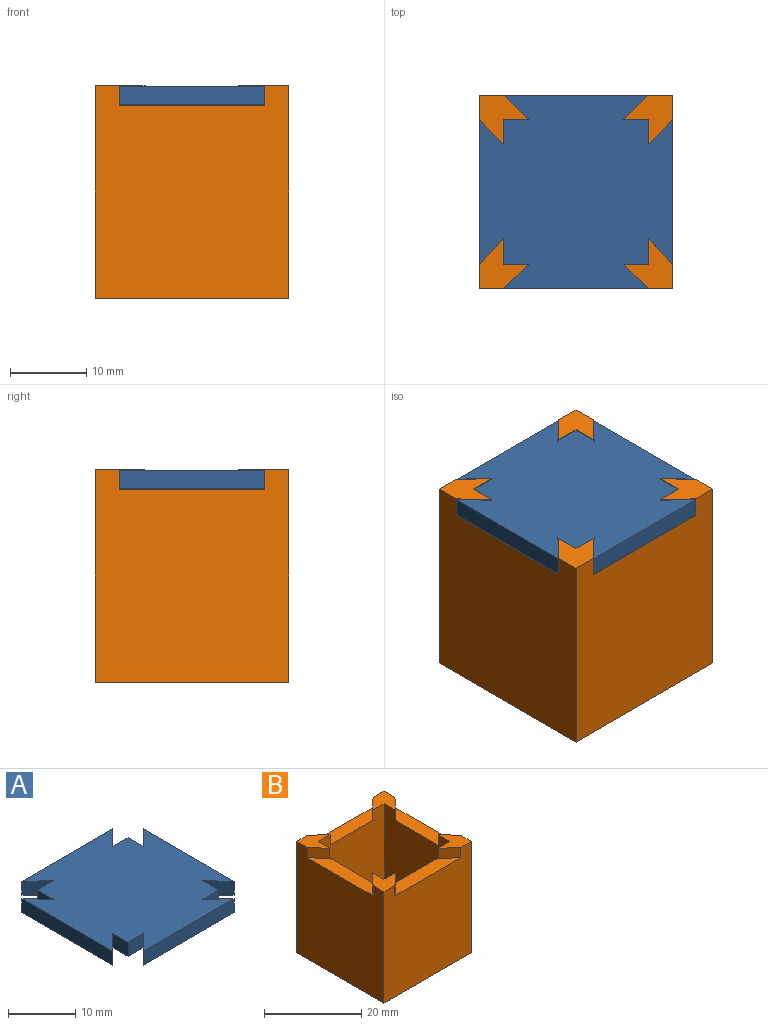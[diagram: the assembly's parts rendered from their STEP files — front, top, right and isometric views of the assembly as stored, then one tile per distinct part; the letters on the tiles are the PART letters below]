
ASSEMBLY  parts=2 mates=1
PART A: 22 faces, bbox 25.4x25.4x2.5 mm
  f0: plane 3.35x3.18mm, normal (-0.69,-0.73,0), area 11.7mm2, adj f1,f19,f20,f21
  f1: plane 3.35x2.54mm, normal (0,1,0), area 8.5mm2, adj f0,f2,f20,f21
  f2: plane 3.35x2.54mm, normal (-1,0,0), area 8.5mm2, adj f1,f3,f20,f21
  f3: plane 3.35x3.18mm, normal (0.73,0.69,0), area 11.7mm2, adj f2,f4,f20,f21
  f4: plane 19.05x2.54mm, normal (-1,0,0), area 48.4mm2, adj f3,f5,f20,f21
  f5: plane 3.35x3.18mm, normal (0.73,-0.69,0), area 11.7mm2, adj f4,f6,f20,f21
  f6: plane 3.35x2.54mm, normal (-1,0,0), area 8.5mm2, adj f5,f7,f20,f21
  f7: plane 3.35x2.54mm, normal (0,-1,0), area 8.5mm2, adj f6,f8,f20,f21
  f8: plane 3.35x3.18mm, normal (-0.69,0.73,0), area 11.7mm2, adj f7,f9,f20,f21
  f9: plane 19.05x2.54mm, normal (0,-1,0), area 48.4mm2, adj f8,f10,f20,f21
  f10: plane 3.35x3.18mm, normal (0.69,0.73,0), area 11.7mm2, adj f9,f11,f20,f21
  f11: plane 3.35x2.54mm, normal (0,-1,0), area 8.5mm2, adj f10,f12,f20,f21
  f12: plane 3.35x2.54mm, normal (1,0,0), area 8.5mm2, adj f11,f13,f20,f21
  f13: plane 3.35x3.18mm, normal (-0.73,-0.69,0), area 11.7mm2, adj f12,f14,f20,f21
  f14: plane 19.05x2.54mm, normal (1,0,0), area 48.4mm2, adj f13,f15,f20,f21
  f15: plane 3.35x3.18mm, normal (-0.73,0.69,0), area 11.7mm2, adj f14,f16,f20,f21
  f16: plane 3.35x2.54mm, normal (1,0,0), area 8.5mm2, adj f15,f17,f20,f21
  f17: plane 3.35x2.54mm, normal (0,1,0), area 8.5mm2, adj f16,f18,f20,f21
  f18: plane 3.35x3.18mm, normal (0.69,-0.73,0), area 11.7mm2, adj f17,f19,f20,f21
  f19: plane 19.05x2.54mm, normal (0,1,0), area 48.4mm2, adj f0,f18,f20,f21
  f20: plane 25.4x25.4mm, normal (0,0,1), area 562.3mm2, adj f0,f1,f2,f3,f4,f5,f6,f7
  f21: plane 25.4x25.4mm, normal (0,0,-1), area 562.3mm2, adj f0,f1,f2,f3,f4,f5,f6,f7
PART B: 26 faces, bbox 25.4x25.4x27.9 mm
  f0: plane 19.05x3.18mm, normal (0,0,1), area 49.8mm2, adj f5,f10,f14,f24
  f1: plane 19.06x3.18mm, normal (0,0,1), area 49.8mm2, adj f8,f9,f20,f23
  f2: plane 19.06x3.18mm, normal (0,0,1), area 49.8mm2, adj f7,f12,f18,f21
  f3: plane 19.05x3.18mm, normal (0,0,1), area 49.8mm2, adj f6,f11,f15,f17
  f4: plane 25.4x25.4mm, normal (0,0,-1), area 645.2mm2, adj f9,f10,f11,f12
  f5: plane 26.35x19.05mm, normal (0,-1,0), area 470.7mm2, adj f0,f6,f8,f13,f14,f16,f24,f25
  f6: plane 26.35x19.05mm, normal (1,0,0), area 470.7mm2, adj f3,f5,f7,f13,f15,f16,f17,f19
  f7: plane 26.35x19.05mm, normal (0,1,0), area 470.7mm2, adj f2,f6,f8,f13,f18,f19,f21,f22
  f8: plane 26.35x19.05mm, normal (-1,0,0), area 470.7mm2, adj f1,f5,f7,f13,f20,f22,f23,f25
  f9: plane 27.94x25.4mm, normal (1,0,0), area 661.3mm2, adj f1,f4,f10,f12,f20,f22,f23,f25
  f10: plane 27.94x25.4mm, normal (0,1,0), area 661.3mm2, adj f0,f4,f9,f11,f14,f16,f24,f25
  f11: plane 27.94x25.4mm, normal (-1,0,0), area 661.3mm2, adj f3,f4,f10,f12,f15,f16,f17,f19
  f12: plane 27.94x25.4mm, normal (0,-1,0), area 661.3mm2, adj f2,f4,f9,f11,f18,f19,f21,f22
  f13: plane 19.05x19.05mm, normal (0,0,1), area 362.9mm2, adj f5,f6,f7,f8
  f14: plane 3.36x3.18mm, normal (0.69,0.73,0), area 11.7mm2, adj f0,f5,f10,f16
  f15: plane 3.35x3.18mm, normal (-0.73,-0.69,0), area 11.7mm2, adj f3,f6,f11,f16
  f16: plane 6.54x6.53mm, normal (0,0,1), area 20.7mm2, adj f5,f6,f10,f11,f14,f15
  f17: plane 3.35x3.18mm, normal (-0.73,0.69,0), area 11.7mm2, adj f3,f6,f11,f19
  f18: plane 3.36x3.18mm, normal (0.69,-0.73,0), area 11.7mm2, adj f2,f7,f12,f19
  f19: plane 6.54x6.53mm, normal (0,0,1), area 20.7mm2, adj f6,f7,f11,f12,f17,f18
  f20: plane 3.36x3.18mm, normal (0.73,0.69,0), area 11.7mm2, adj f1,f8,f9,f22
  f21: plane 3.36x3.18mm, normal (-0.69,-0.73,0), area 11.7mm2, adj f2,f7,f12,f22
  f22: plane 6.54x6.53mm, normal (0,0,1), area 20.7mm2, adj f7,f8,f9,f12,f20,f21
  f23: plane 3.36x3.18mm, normal (0.73,-0.69,0), area 11.7mm2, adj f1,f8,f9,f25
  f24: plane 3.36x3.18mm, normal (-0.69,0.73,0), area 11.7mm2, adj f0,f5,f10,f25
  f25: plane 6.54x6.53mm, normal (0,0,1), area 20.7mm2, adj f5,f8,f9,f10,f23,f24
PLACE A t=(4.66,-9.85,27.48)mm
PLACE B t=(2.9,-11.1,2.19)mm fixed
MATE slider A.f20 <-> B.f25  axis (0,0,1) through (-11.87,7.95,30.02)mm
